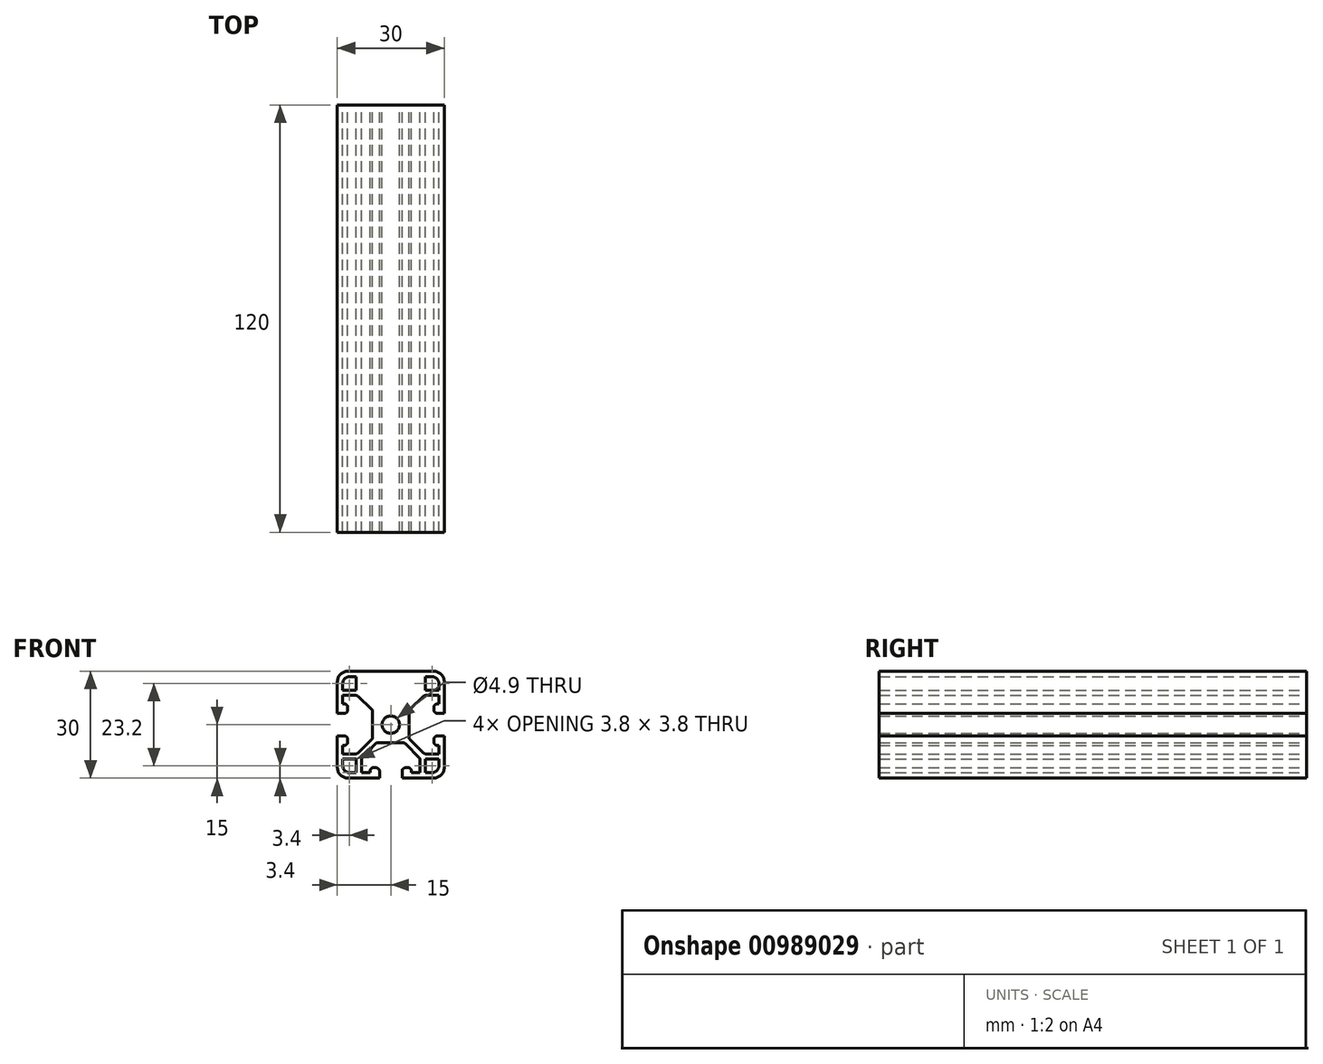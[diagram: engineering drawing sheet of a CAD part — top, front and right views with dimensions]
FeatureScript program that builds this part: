
annotation { "Feature Type Name" : "Feature", "Feature Type Description" : "" }
export const myFeature = defineFeature(function(context is Context, id is Id, definition is map)
    precondition{}
    {
        {
            var Q0;
            Q0=qCreatedBy(makeId("Front.planeOp"),FACE);
            var sketch = newSketch(context, id + "F0", { "sketchPlane" : qUnion([Q0])});
            skLineSegment(sketch, "E0.bottom", {"start": v(-12, 15) * mm, "end": v(12, 15) * mm});
            skLineSegment(sketch, "E0.top", {"start": v(-12, -15) * mm, "end": v(12, -15) * mm});
            skLineSegment(sketch, "E0.left", {"start": v(-15, 12) * mm, "end": v(-15, -12) * mm});
            skLineSegment(sketch, "E0.right", {"start": v(15, 12) * mm, "end": v(15, -12) * mm});
            skPoint(sketch, "E1.visualSharp", {"position": v(-15, 15) * mm});
            skArc(sketch, "E1.filletArc", {"start": v(-12, 15) * mm, "mid": v(-14.12, 14.12) * mm, "end": v(-15, 12) * mm});
            skPoint(sketch, "E2.visualSharp", {"position": v(15, 15) * mm});
            skArc(sketch, "E2.filletArc", {"start": v(15, 12) * mm, "mid": v(14.12, 14.12) * mm, "end": v(12, 15) * mm});
            skPoint(sketch, "E3.visualSharp", {"position": v(15, -15) * mm});
            skArc(sketch, "E3.filletArc", {"start": v(12, -15) * mm, "mid": v(14.12, -14.12) * mm, "end": v(15, -12) * mm});
            skPoint(sketch, "E4.visualSharp", {"position": v(-15, -15) * mm});
            skArc(sketch, "E4.filletArc", {"start": v(-15, -12) * mm, "mid": v(-14.12, -14.12) * mm, "end": v(-12, -15) * mm});
            skCircle(sketch, "E5", {"center": v(0, 0) * mm, "radius": 2.45 * mm});
            skPoint(sketch, "E6", {"position": v(15, 8.22) * mm});
            skPoint(sketch, "E7", {"position": v(15, -8.22) * mm});
            skPoint(sketch, "E8", {"position": v(15, 3.17) * mm});
            skPoint(sketch, "E9", {"position": v(15, -3.18) * mm});
            skLineSegment(sketch, "E10", {"start": v(15, 3.17) * mm, "end": v(13.09, 3.17) * mm});
            skLineSegment(sketch, "E11", {"start": v(13.09, -3.18) * mm, "end": v(15, -3.18) * mm});
            skPoint(sketch, "E12", {"position": v(12.06, -5.83) * mm});
            skPoint(sketch, "E13", {"position": v(12.06, 5.82) * mm});
            skPoint(sketch, "E14", {"position": v(13.5, -5.82) * mm});
            skPoint(sketch, "E15", {"position": v(13.5, 5.82) * mm});
            skPoint(sketch, "E16", {"position": v(13.5, 8.22) * mm});
            skPoint(sketch, "E17", {"position": v(13.5, -8.22) * mm});
            skPoint(sketch, "E18", {"position": v(9.5, 8.22) * mm});
            skPoint(sketch, "E19", {"position": v(9.5, -8.22) * mm});
            skPoint(sketch, "E20", {"position": v(5.1, -3.92) * mm});
            skPoint(sketch, "E21", {"position": v(5.1, 4.08) * mm});
            skLineSegment(sketch, "E22", {"start": v(12.09, -4.16) * mm, "end": v(12.08, -4.81) * mm});
            skLineSegment(sketch, "E23", {"start": v(13.5, -5.82) * mm, "end": v(13.5, -8.22) * mm});
            skLineSegment(sketch, "E24", {"start": v(9.2, -7.94) * mm, "end": v(5.4, -4.21) * mm});
            skLineSegment(sketch, "E25", {"start": v(5.1, 3.65) * mm, "end": v(5.1, -3.5) * mm});
            skLineSegment(sketch, "E26", {"start": v(5.41, 4.38) * mm, "end": v(9.21, 7.95) * mm});
            skLineSegment(sketch, "E27", {"start": v(13.5, 8.22) * mm, "end": v(9.9, 8.22) * mm});
            skLineSegment(sketch, "E28", {"start": v(13.5, 8.22) * mm, "end": v(13.5, 5.82) * mm});
            skLineSegment(sketch, "E29", {"start": v(13.08, 5.82) * mm, "end": v(13.5, 5.82) * mm});
            skLineSegment(sketch, "E30", {"start": v(12.08, 4.81) * mm, "end": v(12.09, 4.16) * mm});
            skLineSegment(sketch, "E31", {"start": v(13.08, -5.83) * mm, "end": v(13.5, -5.83) * mm});
            skLineSegment(sketch, "E32", {"start": v(13.5, -8.22) * mm, "end": v(9.9, -8.22) * mm});
            skLineSegment(sketch, "E33", {"start": v(13.5, -8.22) * mm, "end": v(13.5, -5.82) * mm});
            skArc(sketch, "E34.filletArc", {"start": v(9.9, 8.22) * mm, "mid": v(9.53, 8.15) * mm, "end": v(9.21, 7.95) * mm});
            skArc(sketch, "E35.filletArc", {"start": v(5.41, 4.38) * mm, "mid": v(5.18, 4.04) * mm, "end": v(5.1, 3.65) * mm});
            skArc(sketch, "E36.filletArc", {"start": v(5.1, -3.5) * mm, "mid": v(5.18, -3.89) * mm, "end": v(5.4, -4.21) * mm});
            skArc(sketch, "E37.filletArc", {"start": v(9.2, -7.94) * mm, "mid": v(9.53, -8.15) * mm, "end": v(9.9, -8.22) * mm});
            skArc(sketch, "E38.filletArc", {"start": v(12.08, -4.81) * mm, "mid": v(12.36, -5.53) * mm, "end": v(13.08, -5.83) * mm});
            skPoint(sketch, "E39.visualSharp", {"position": v(12.1, -3.18) * mm});
            skArc(sketch, "E39.filletArc", {"start": v(13.09, -3.18) * mm, "mid": v(12.38, -3.46) * mm, "end": v(12.09, -4.16) * mm});
            skPoint(sketch, "E40.visualSharp", {"position": v(12.1, 3.17) * mm});
            skArc(sketch, "E40.filletArc", {"start": v(12.09, 4.16) * mm, "mid": v(12.38, 3.46) * mm, "end": v(13.09, 3.17) * mm});
            skArc(sketch, "E41.filletArc", {"start": v(13.08, 5.82) * mm, "mid": v(12.36, 5.53) * mm, "end": v(12.08, 4.81) * mm});
            skArc(sketch, "E42.MirrorCS", {"start": v(-5.1, -3.5) * mm, "mid": v(-5.18, -3.89) * mm, "end": v(-5.4, -4.21) * mm});
            skLineSegment(sketch, "E43.MirrorCS", {"start": v(-13.08, -5.83) * mm, "end": v(-13.5, -5.83) * mm});
            skArc(sketch, "E44.MirrorCS", {"start": v(-9.2, -7.94) * mm, "mid": v(-9.53, -8.15) * mm, "end": v(-9.9, -8.22) * mm});
            skLineSegment(sketch, "E45.MirrorCS", {"start": v(-13.08, 5.82) * mm, "end": v(-13.5, 5.82) * mm});
            skArc(sketch, "E46.MirrorCS", {"start": v(-5.41, 4.38) * mm, "mid": v(-5.18, 4.04) * mm, "end": v(-5.1, 3.65) * mm});
            skArc(sketch, "E47.MirrorCS", {"start": v(-9.9, 8.22) * mm, "mid": v(-9.53, 8.15) * mm, "end": v(-9.21, 7.95) * mm});
            skArc(sketch, "E48.MirrorCS", {"start": v(-13.08, 5.82) * mm, "mid": v(-12.36, 5.53) * mm, "end": v(-12.08, 4.81) * mm});
            skLineSegment(sketch, "E49.MirrorCS", {"start": v(-12.08, 4.81) * mm, "end": v(-12.09, 4.16) * mm});
            skLineSegment(sketch, "E50.MirrorCS", {"start": v(-12.09, -4.16) * mm, "end": v(-12.08, -4.81) * mm});
            skArc(sketch, "E51.MirrorCS", {"start": v(-12.08, -4.81) * mm, "mid": v(-12.36, -5.53) * mm, "end": v(-13.08, -5.83) * mm});
            skLineSegment(sketch, "E52.MirrorCS", {"start": v(-13.5, -8.22) * mm, "end": v(-13.5, -5.82) * mm});
            skLineSegment(sketch, "E53.MirrorCS", {"start": v(-13.5, -5.82) * mm, "end": v(-13.5, -8.22) * mm});
            skLineSegment(sketch, "E54.MirrorCS", {"start": v(-13.09, -3.18) * mm, "end": v(-15, -3.18) * mm});
            skArc(sketch, "E55.MirrorCS", {"start": v(-12.09, 4.16) * mm, "mid": v(-12.38, 3.46) * mm, "end": v(-13.09, 3.17) * mm});
            skArc(sketch, "E56.MirrorCS", {"start": v(-13.09, -3.18) * mm, "mid": v(-12.38, -3.46) * mm, "end": v(-12.09, -4.16) * mm});
            skLineSegment(sketch, "E57.MirrorCS", {"start": v(-15, 3.17) * mm, "end": v(-13.09, 3.17) * mm});
            skPoint(sketch, "E58.MirrorP", {"position": v(-5.1, -3.92) * mm});
            skPoint(sketch, "E59.MirrorP", {"position": v(-9.5, -8.22) * mm});
            skPoint(sketch, "E60.MirrorP", {"position": v(-13.5, -8.22) * mm});
            skPoint(sketch, "E61.MirrorP", {"position": v(-12.06, 5.82) * mm});
            skPoint(sketch, "E62.MirrorP", {"position": v(-5.1, 4.08) * mm});
            skLineSegment(sketch, "E63.MirrorCS", {"start": v(-13.5, 8.22) * mm, "end": v(-13.5, 5.82) * mm});
            skPoint(sketch, "E64.MirrorP", {"position": v(-12.06, -5.83) * mm});
            skPoint(sketch, "E65.MirrorP", {"position": v(-9.5, 8.22) * mm});
            skPoint(sketch, "E66.MirrorP", {"position": v(-15, 8.22) * mm});
            skPoint(sketch, "E67.MirrorP", {"position": v(-13.5, 5.82) * mm});
            skLineSegment(sketch, "E68.MirrorCS", {"start": v(-13.5, 8.22) * mm, "end": v(-9.9, 8.22) * mm});
            skPoint(sketch, "E69.MirrorP", {"position": v(-13.5, -5.82) * mm});
            skLineSegment(sketch, "E70.MirrorCS", {"start": v(-13.5, -8.22) * mm, "end": v(-9.9, -8.22) * mm});
            skLineSegment(sketch, "E71.MirrorCS", {"start": v(-5.1, 3.65) * mm, "end": v(-5.1, -3.5) * mm});
            skPoint(sketch, "E72.MirrorP", {"position": v(-13.5, 8.22) * mm});
            skPoint(sketch, "E73.MirrorP", {"position": v(-15, -3.18) * mm});
            skPoint(sketch, "E74.MirrorP", {"position": v(-12.1, 3.17) * mm});
            skPoint(sketch, "E75.MirrorP", {"position": v(-15, -8.22) * mm});
            skPoint(sketch, "E76.MirrorP", {"position": v(-12.1, -3.18) * mm});
            skLineSegment(sketch, "E77.MirrorCS", {"start": v(-5.41, 4.38) * mm, "end": v(-9.21, 7.95) * mm});
            skLineSegment(sketch, "E78.MirrorCS", {"start": v(-9.2, -7.94) * mm, "end": v(-5.4, -4.21) * mm});
            skPoint(sketch, "E79.MirrorP", {"position": v(-15, 3.17) * mm});
            skArc(sketch, "E80.MirrorCS", {"start": v(-3.5, 5.1) * mm, "mid": v(-3.89, 5.18) * mm, "end": v(-4.21, 5.4) * mm});
            skLineSegment(sketch, "E81.MirrorCS", {"start": v(-5.82, 13.08) * mm, "end": v(-5.82, 13.5) * mm});
            skArc(sketch, "E82.MirrorCS", {"start": v(-7.94, 9.2) * mm, "mid": v(-8.15, 9.53) * mm, "end": v(-8.22, 9.9) * mm});
            skLineSegment(sketch, "E83.MirrorCS", {"start": v(5.83, 13.08) * mm, "end": v(5.83, 13.5) * mm});
            skArc(sketch, "E84.MirrorCS", {"start": v(4.38, 5.41) * mm, "mid": v(4.04, 5.18) * mm, "end": v(3.65, 5.1) * mm});
            skArc(sketch, "E85.MirrorCS", {"start": v(8.23, 9.9) * mm, "mid": v(8.15, 9.53) * mm, "end": v(7.95, 9.21) * mm});
            skArc(sketch, "E86.MirrorCS", {"start": v(5.83, 13.08) * mm, "mid": v(5.53, 12.36) * mm, "end": v(4.81, 12.08) * mm});
            skLineSegment(sketch, "E87.MirrorCS", {"start": v(4.81, 12.08) * mm, "end": v(4.16, 12.09) * mm});
            skLineSegment(sketch, "E88.MirrorCS", {"start": v(-4.16, 12.09) * mm, "end": v(-4.81, 12.08) * mm});
            skArc(sketch, "E89.MirrorCS", {"start": v(-4.81, 12.08) * mm, "mid": v(-5.53, 12.36) * mm, "end": v(-5.82, 13.08) * mm});
            skLineSegment(sketch, "E90.MirrorCS", {"start": v(-8.22, 13.5) * mm, "end": v(-5.82, 13.5) * mm});
            skLineSegment(sketch, "E91.MirrorCS", {"start": v(-5.82, 13.5) * mm, "end": v(-8.22, 13.5) * mm});
            skLineSegment(sketch, "E92.MirrorCS", {"start": v(-3.17, 13.09) * mm, "end": v(-3.17, 15) * mm});
            skArc(sketch, "E93.MirrorCS", {"start": v(4.16, 12.09) * mm, "mid": v(3.46, 12.38) * mm, "end": v(3.18, 13.09) * mm});
            skArc(sketch, "E94.MirrorCS", {"start": v(-3.17, 13.09) * mm, "mid": v(-3.46, 12.38) * mm, "end": v(-4.16, 12.09) * mm});
            skLineSegment(sketch, "E95.MirrorCS", {"start": v(3.18, 15) * mm, "end": v(3.18, 13.09) * mm});
            skPoint(sketch, "E96.MirrorP", {"position": v(-3.92, 5.1) * mm});
            skPoint(sketch, "E97.MirrorP", {"position": v(-8.22, 9.5) * mm});
            skPoint(sketch, "E98.MirrorP", {"position": v(-8.22, 13.5) * mm});
            skPoint(sketch, "E99.MirrorP", {"position": v(5.83, 12.06) * mm});
            skPoint(sketch, "E100.MirrorP", {"position": v(4.08, 5.1) * mm});
            skLineSegment(sketch, "E101.MirrorCS", {"start": v(8.23, 13.5) * mm, "end": v(5.83, 13.5) * mm});
            skPoint(sketch, "E102.MirrorP", {"position": v(-5.82, 12.06) * mm});
            skPoint(sketch, "E103.MirrorP", {"position": v(8.23, 9.5) * mm});
            skPoint(sketch, "E104.MirrorP", {"position": v(8.23, 15) * mm});
            skPoint(sketch, "E105.MirrorP", {"position": v(5.83, 13.5) * mm});
            skLineSegment(sketch, "E106.MirrorCS", {"start": v(8.23, 13.5) * mm, "end": v(8.23, 9.9) * mm});
            skPoint(sketch, "E107.MirrorP", {"position": v(-5.82, 13.5) * mm});
            skLineSegment(sketch, "E108.MirrorCS", {"start": v(-8.22, 13.5) * mm, "end": v(-8.22, 9.9) * mm});
            skLineSegment(sketch, "E109.MirrorCS", {"start": v(3.65, 5.1) * mm, "end": v(-3.5, 5.1) * mm});
            skPoint(sketch, "E110.MirrorP", {"position": v(8.23, 13.5) * mm});
            skPoint(sketch, "E111.MirrorP", {"position": v(-3.17, 15) * mm});
            skPoint(sketch, "E112.MirrorP", {"position": v(3.18, 12.1) * mm});
            skPoint(sketch, "E113.MirrorP", {"position": v(-8.22, 15) * mm});
            skPoint(sketch, "E114.MirrorP", {"position": v(-3.17, 12.1) * mm});
            skLineSegment(sketch, "E115.MirrorCS", {"start": v(4.38, 5.41) * mm, "end": v(7.95, 9.21) * mm});
            skLineSegment(sketch, "E116.MirrorCS", {"start": v(-7.94, 9.2) * mm, "end": v(-4.21, 5.4) * mm});
            skPoint(sketch, "E117.MirrorP", {"position": v(3.18, 15) * mm});
            skPoint(sketch, "E118", {"position": v(-8.22, -15) * mm});
            skArc(sketch, "E119.MirrorCS", {"start": v(3.5, -5.1) * mm, "mid": v(3.89, -5.18) * mm, "end": v(4.21, -5.4) * mm});
            skLineSegment(sketch, "E120.MirrorCS", {"start": v(5.83, -13.08) * mm, "end": v(5.83, -13.5) * mm});
            skArc(sketch, "E121.MirrorCS", {"start": v(7.94, -9.2) * mm, "mid": v(8.15, -9.53) * mm, "end": v(8.23, -9.9) * mm});
            skLineSegment(sketch, "E122.MirrorCS", {"start": v(-5.82, -13.08) * mm, "end": v(-5.82, -13.5) * mm});
            skArc(sketch, "E123.MirrorCS", {"start": v(-4.38, -5.41) * mm, "mid": v(-4.04, -5.18) * mm, "end": v(-3.65, -5.1) * mm});
            skArc(sketch, "E124.MirrorCS", {"start": v(-8.22, -9.9) * mm, "mid": v(-8.15, -9.53) * mm, "end": v(-7.95, -9.21) * mm});
            skArc(sketch, "E125.MirrorCS", {"start": v(-5.82, -13.08) * mm, "mid": v(-5.53, -12.36) * mm, "end": v(-4.81, -12.08) * mm});
            skLineSegment(sketch, "E126.MirrorCS", {"start": v(-4.81, -12.08) * mm, "end": v(-4.16, -12.09) * mm});
            skLineSegment(sketch, "E127.MirrorCS", {"start": v(4.16, -12.09) * mm, "end": v(4.81, -12.08) * mm});
            skArc(sketch, "E128.MirrorCS", {"start": v(4.81, -12.08) * mm, "mid": v(5.53, -12.36) * mm, "end": v(5.83, -13.08) * mm});
            skLineSegment(sketch, "E129.MirrorCS", {"start": v(8.23, -13.5) * mm, "end": v(5.83, -13.5) * mm});
            skLineSegment(sketch, "E130.MirrorCS", {"start": v(5.83, -13.5) * mm, "end": v(8.23, -13.5) * mm});
            skLineSegment(sketch, "E131.MirrorCS", {"start": v(3.18, -13.09) * mm, "end": v(3.18, -15) * mm});
            skArc(sketch, "E132.MirrorCS", {"start": v(-4.16, -12.09) * mm, "mid": v(-3.46, -12.38) * mm, "end": v(-3.17, -13.09) * mm});
            skArc(sketch, "E133.MirrorCS", {"start": v(3.18, -13.09) * mm, "mid": v(3.46, -12.38) * mm, "end": v(4.16, -12.09) * mm});
            skLineSegment(sketch, "E134.MirrorCS", {"start": v(-3.17, -15) * mm, "end": v(-3.17, -13.09) * mm});
            skPoint(sketch, "E135.MirrorP", {"position": v(3.92, -5.1) * mm});
            skPoint(sketch, "E136.MirrorP", {"position": v(8.23, -9.5) * mm});
            skPoint(sketch, "E137.MirrorP", {"position": v(8.23, -13.5) * mm});
            skPoint(sketch, "E138.MirrorP", {"position": v(-5.82, -12.06) * mm});
            skPoint(sketch, "E139.MirrorP", {"position": v(-4.08, -5.1) * mm});
            skLineSegment(sketch, "E140.MirrorCS", {"start": v(-8.22, -13.5) * mm, "end": v(-5.82, -13.5) * mm});
            skPoint(sketch, "E141.MirrorP", {"position": v(5.83, -12.06) * mm});
            skPoint(sketch, "E142.MirrorP", {"position": v(-8.22, -9.5) * mm});
            skPoint(sketch, "E143.MirrorP", {"position": v(-5.82, -13.5) * mm});
            skLineSegment(sketch, "E144.MirrorCS", {"start": v(-8.22, -13.5) * mm, "end": v(-8.22, -9.9) * mm});
            skPoint(sketch, "E145.MirrorP", {"position": v(5.83, -13.5) * mm});
            skLineSegment(sketch, "E146.MirrorCS", {"start": v(8.23, -13.5) * mm, "end": v(8.23, -9.9) * mm});
            skLineSegment(sketch, "E147.MirrorCS", {"start": v(-3.65, -5.1) * mm, "end": v(3.5, -5.1) * mm});
            skPoint(sketch, "E148.MirrorP", {"position": v(-8.22, -13.5) * mm});
            skPoint(sketch, "E149.MirrorP", {"position": v(3.18, -15) * mm});
            skPoint(sketch, "E150.MirrorP", {"position": v(-3.17, -12.1) * mm});
            skPoint(sketch, "E151.MirrorP", {"position": v(8.23, -15) * mm});
            skPoint(sketch, "E152.MirrorP", {"position": v(3.18, -12.1) * mm});
            skLineSegment(sketch, "E153.MirrorCS", {"start": v(-4.38, -5.41) * mm, "end": v(-7.95, -9.21) * mm});
            skLineSegment(sketch, "E154.MirrorCS", {"start": v(7.94, -9.2) * mm, "end": v(4.21, -5.4) * mm});
            skPoint(sketch, "E155.MirrorP", {"position": v(-3.17, -15) * mm});
            skLineSegment(sketch, "E156.bottom", {"start": v(-13.5, -9.7) * mm, "end": v(-9.7, -9.7) * mm});
            skLineSegment(sketch, "E156.top", {"start": v(-11.5, -13.5) * mm, "end": v(-9.7, -13.5) * mm});
            skLineSegment(sketch, "E156.left", {"start": v(-13.5, -9.7) * mm, "end": v(-13.5, -11.5) * mm});
            skLineSegment(sketch, "E156.right", {"start": v(-9.7, -9.7) * mm, "end": v(-9.7, -13.5) * mm});
            skPoint(sketch, "E157.visualSharp", {"position": v(-13.5, -13.5) * mm});
            skArc(sketch, "E157.filletArc", {"start": v(-13.5, -11.5) * mm, "mid": v(-12.91, -12.91) * mm, "end": v(-11.5, -13.5) * mm});
            skPoint(sketch, "E158", {"position": v(-11.6, -11.6) * mm});
            skPoint(sketch, "E159.MirrorP", {"position": v(-11.6, 11.6) * mm});
            skLineSegment(sketch, "E160.MirrorCS", {"start": v(-11.5, 13.5) * mm, "end": v(-9.7, 13.5) * mm});
            skLineSegment(sketch, "E161.MirrorCS", {"start": v(-9.7, 9.7) * mm, "end": v(-9.7, 13.5) * mm});
            skLineSegment(sketch, "E162.MirrorCS", {"start": v(-13.5, 9.7) * mm, "end": v(-9.7, 9.7) * mm});
            skLineSegment(sketch, "E163.MirrorCS", {"start": v(-13.5, 9.7) * mm, "end": v(-13.5, 11.5) * mm});
            skPoint(sketch, "E164.MirrorP", {"position": v(-13.5, 13.5) * mm});
            skArc(sketch, "E165.MirrorCS", {"start": v(-13.5, 11.5) * mm, "mid": v(-12.91, 12.91) * mm, "end": v(-11.5, 13.5) * mm});
            skPoint(sketch, "E166.MirrorP", {"position": v(11.6, 11.6) * mm});
            skLineSegment(sketch, "E167.MirrorCS", {"start": v(11.5, 13.5) * mm, "end": v(9.7, 13.5) * mm});
            skLineSegment(sketch, "E168.MirrorCS", {"start": v(13.5, 9.7) * mm, "end": v(9.7, 9.7) * mm});
            skLineSegment(sketch, "E169.MirrorCS", {"start": v(9.7, 9.7) * mm, "end": v(9.7, 13.5) * mm});
            skLineSegment(sketch, "E170.MirrorCS", {"start": v(13.5, 9.7) * mm, "end": v(13.5, 11.5) * mm});
            skArc(sketch, "E171.MirrorCS", {"start": v(13.5, 11.5) * mm, "mid": v(12.91, 12.91) * mm, "end": v(11.5, 13.5) * mm});
            skPoint(sketch, "E172.MirrorP", {"position": v(11.6, -11.6) * mm});
            skLineSegment(sketch, "E173.MirrorCS", {"start": v(13.5, -9.7) * mm, "end": v(13.5, -11.5) * mm});
            skArc(sketch, "E174.MirrorCS", {"start": v(13.5, -11.5) * mm, "mid": v(12.91, -12.91) * mm, "end": v(11.5, -13.5) * mm});
            skLineSegment(sketch, "E175.MirrorCS", {"start": v(13.5, -9.7) * mm, "end": v(9.7, -9.7) * mm});
            skLineSegment(sketch, "E176.MirrorCS", {"start": v(9.7, -9.7) * mm, "end": v(9.7, -13.5) * mm});
            skLineSegment(sketch, "E177.MirrorCS", {"start": v(11.5, -13.5) * mm, "end": v(9.7, -13.5) * mm});
            skSolve(sketch);
        }
        {
            var Q0;
            {var subQ13=sQuery(id+"F0.wireOp",EDGE,"E1.filletArc");Q0=makeQuery(id+"F0.imprint","IMPRINT",FACE,{"disambiguationData":[TD([[makeQuery(id+"F0.imprint","IMPRINT",EDGE,{"derivedFrom":subQ13}),1.0]])]});}
            extrude(context, id + "F1", {"entities" : qUnion([Q0]), "depth" : 460 * mm, "offsetDistance" : 25 * mm});
        }
        {
            var Q0;
            Q0=makeQuery(id+"F1.opExtrude","CAP_FACE",FACE,{"disambiguationData":[OSD([sQuery(id+"F0.wireOp",EDGE,"E0.bottom"),sQuery(id+"F0.wireOp",EDGE,"E0.top"),sQuery(id+"F0.wireOp",EDGE,"E0.left"),sQuery(id+"F0.wireOp",EDGE,"E0.right"),sQuery(id+"F0.wireOp",EDGE,"E1.filletArc"),sQuery(id+"F0.wireOp",EDGE,"E2.filletArc"),sQuery(id+"F0.wireOp",EDGE,"E3.filletArc"),sQuery(id+"F0.wireOp",EDGE,"E4.filletArc"),sQuery(id+"F0.wireOp",EDGE,"E5"),sQuery(id+"F0.wireOp",EDGE,"E10"),sQuery(id+"F0.wireOp",EDGE,"E11"),sQuery(id+"F0.wireOp",EDGE,"E22"),sQuery(id+"F0.wireOp",EDGE,"E24"),sQuery(id+"F0.wireOp",EDGE,"E25"),sQuery(id+"F0.wireOp",EDGE,"E26"),sQuery(id+"F0.wireOp",EDGE,"E27"),sQuery(id+"F0.wireOp",EDGE,"E28"),sQuery(id+"F0.wireOp",EDGE,"E29"),sQuery(id+"F0.wireOp",EDGE,"E30"),sQuery(id+"F0.wireOp",EDGE,"E31"),sQuery(id+"F0.wireOp",EDGE,"E32"),sQuery(id+"F0.wireOp",EDGE,"E33"),sQuery(id+"F0.wireOp",EDGE,"E34.filletArc"),sQuery(id+"F0.wireOp",EDGE,"E35.filletArc"),sQuery(id+"F0.wireOp",EDGE,"E36.filletArc"),sQuery(id+"F0.wireOp",EDGE,"E37.filletArc"),sQuery(id+"F0.wireOp",EDGE,"E38.filletArc"),sQuery(id+"F0.wireOp",EDGE,"E39.filletArc"),sQuery(id+"F0.wireOp",EDGE,"E40.filletArc"),sQuery(id+"F0.wireOp",EDGE,"E41.filletArc"),sQuery(id+"F0.wireOp",EDGE,"E42.MirrorCS"),sQuery(id+"F0.wireOp",EDGE,"E43.MirrorCS"),sQuery(id+"F0.wireOp",EDGE,"E44.MirrorCS"),sQuery(id+"F0.wireOp",EDGE,"E45.MirrorCS"),sQuery(id+"F0.wireOp",EDGE,"E46.MirrorCS"),sQuery(id+"F0.wireOp",EDGE,"E47.MirrorCS"),sQuery(id+"F0.wireOp",EDGE,"E48.MirrorCS"),sQuery(id+"F0.wireOp",EDGE,"E49.MirrorCS"),sQuery(id+"F0.wireOp",EDGE,"E50.MirrorCS"),sQuery(id+"F0.wireOp",EDGE,"E51.MirrorCS"),sQuery(id+"F0.wireOp",EDGE,"E53.MirrorCS"),sQuery(id+"F0.wireOp",EDGE,"E54.MirrorCS"),sQuery(id+"F0.wireOp",EDGE,"E55.MirrorCS"),sQuery(id+"F0.wireOp",EDGE,"E56.MirrorCS"),sQuery(id+"F0.wireOp",EDGE,"E57.MirrorCS"),sQuery(id+"F0.wireOp",EDGE,"E63.MirrorCS"),sQuery(id+"F0.wireOp",EDGE,"E68.MirrorCS"),sQuery(id+"F0.wireOp",EDGE,"E70.MirrorCS"),sQuery(id+"F0.wireOp",EDGE,"E71.MirrorCS"),sQuery(id+"F0.wireOp",EDGE,"E77.MirrorCS"),sQuery(id+"F0.wireOp",EDGE,"E78.MirrorCS"),sQuery(id+"F0.wireOp",EDGE,"E80.MirrorCS"),sQuery(id+"F0.wireOp",EDGE,"E81.MirrorCS"),sQuery(id+"F0.wireOp",EDGE,"E82.MirrorCS"),sQuery(id+"F0.wireOp",EDGE,"E83.MirrorCS"),sQuery(id+"F0.wireOp",EDGE,"E84.MirrorCS"),sQuery(id+"F0.wireOp",EDGE,"E85.MirrorCS"),sQuery(id+"F0.wireOp",EDGE,"E86.MirrorCS"),sQuery(id+"F0.wireOp",EDGE,"E87.MirrorCS"),sQuery(id+"F0.wireOp",EDGE,"E88.MirrorCS"),sQuery(id+"F0.wireOp",EDGE,"E89.MirrorCS"),sQuery(id+"F0.wireOp",EDGE,"E91.MirrorCS"),sQuery(id+"F0.wireOp",EDGE,"E92.MirrorCS"),sQuery(id+"F0.wireOp",EDGE,"E93.MirrorCS"),sQuery(id+"F0.wireOp",EDGE,"E94.MirrorCS"),sQuery(id+"F0.wireOp",EDGE,"E95.MirrorCS"),sQuery(id+"F0.wireOp",EDGE,"E101.MirrorCS"),sQuery(id+"F0.wireOp",EDGE,"E106.MirrorCS"),sQuery(id+"F0.wireOp",EDGE,"E108.MirrorCS"),sQuery(id+"F0.wireOp",EDGE,"E109.MirrorCS"),sQuery(id+"F0.wireOp",EDGE,"E115.MirrorCS"),sQuery(id+"F0.wireOp",EDGE,"E116.MirrorCS"),sQuery(id+"F0.wireOp",EDGE,"E119.MirrorCS"),sQuery(id+"F0.wireOp",EDGE,"E120.MirrorCS"),sQuery(id+"F0.wireOp",EDGE,"E121.MirrorCS"),sQuery(id+"F0.wireOp",EDGE,"E122.MirrorCS"),sQuery(id+"F0.wireOp",EDGE,"E123.MirrorCS"),sQuery(id+"F0.wireOp",EDGE,"E124.MirrorCS"),sQuery(id+"F0.wireOp",EDGE,"E125.MirrorCS"),sQuery(id+"F0.wireOp",EDGE,"E126.MirrorCS"),sQuery(id+"F0.wireOp",EDGE,"E127.MirrorCS"),sQuery(id+"F0.wireOp",EDGE,"E128.MirrorCS"),sQuery(id+"F0.wireOp",EDGE,"E130.MirrorCS"),sQuery(id+"F0.wireOp",EDGE,"E131.MirrorCS"),sQuery(id+"F0.wireOp",EDGE,"E132.MirrorCS"),sQuery(id+"F0.wireOp",EDGE,"E133.MirrorCS"),sQuery(id+"F0.wireOp",EDGE,"E134.MirrorCS"),sQuery(id+"F0.wireOp",EDGE,"E140.MirrorCS"),sQuery(id+"F0.wireOp",EDGE,"E144.MirrorCS"),sQuery(id+"F0.wireOp",EDGE,"E146.MirrorCS"),sQuery(id+"F0.wireOp",EDGE,"E147.MirrorCS"),sQuery(id+"F0.wireOp",EDGE,"E153.MirrorCS"),sQuery(id+"F0.wireOp",EDGE,"E154.MirrorCS"),sQuery(id+"F0.wireOp",EDGE,"E160.MirrorCS"),sQuery(id+"F0.wireOp",EDGE,"E161.MirrorCS"),sQuery(id+"F0.wireOp",EDGE,"E162.MirrorCS"),sQuery(id+"F0.wireOp",EDGE,"E163.MirrorCS"),sQuery(id+"F0.wireOp",EDGE,"E165.MirrorCS"),sQuery(id+"F0.wireOp",EDGE,"E156.top"),sQuery(id+"F0.wireOp",EDGE,"E156.bottom"),sQuery(id+"F0.wireOp",EDGE,"E156.right"),sQuery(id+"F0.wireOp",EDGE,"E156.left"),sQuery(id+"F0.wireOp",EDGE,"E157.filletArc"),sQuery(id+"F0.wireOp",EDGE,"E167.MirrorCS"),sQuery(id+"F0.wireOp",EDGE,"E168.MirrorCS"),sQuery(id+"F0.wireOp",EDGE,"E169.MirrorCS"),sQuery(id+"F0.wireOp",EDGE,"E170.MirrorCS"),sQuery(id+"F0.wireOp",EDGE,"E171.MirrorCS"),sQuery(id+"F0.wireOp",EDGE,"E173.MirrorCS"),sQuery(id+"F0.wireOp",EDGE,"E174.MirrorCS"),sQuery(id+"F0.wireOp",EDGE,"E175.MirrorCS"),sQuery(id+"F0.wireOp",EDGE,"E176.MirrorCS"),sQuery(id+"F0.wireOp",EDGE,"E177.MirrorCS")])],"isStart":false});
            extrude(context, id + "F2", {"entities" : qUnion([Q0]), "operationType" : NewBodyOperationType.REMOVE, "oppositeDirection" : true, "depth" : 340 * mm, "offsetDistance" : 25 * mm});
        }
    });
